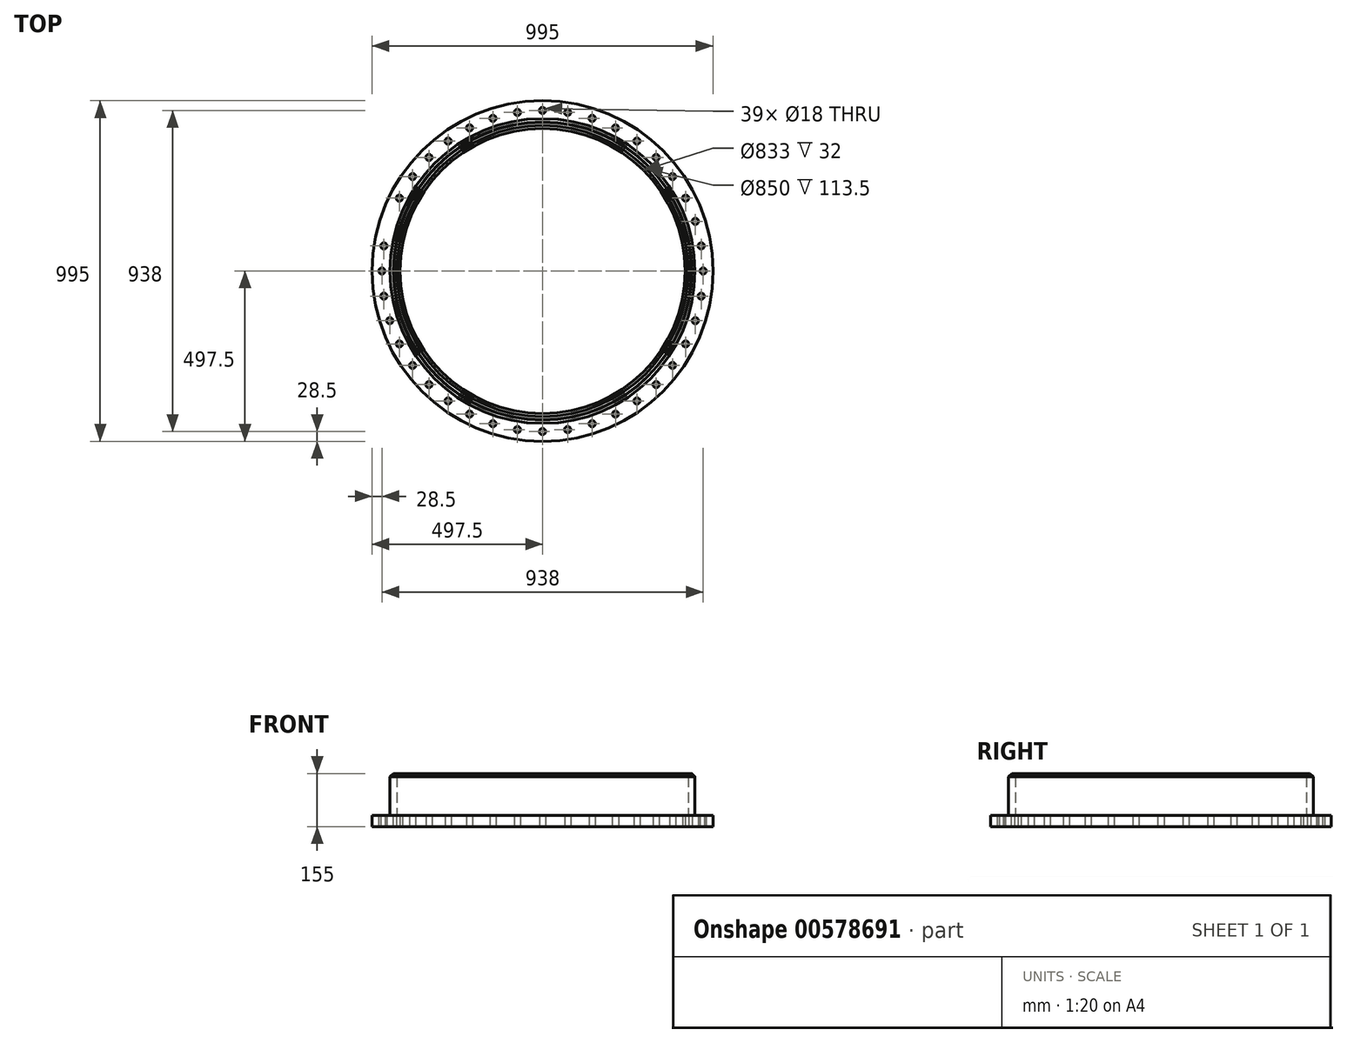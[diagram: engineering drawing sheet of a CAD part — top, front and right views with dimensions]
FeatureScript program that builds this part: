
annotation { "Feature Type Name" : "Feature", "Feature Type Description" : "" }
export const myFeature = defineFeature(function(context is Context, id is Id, definition is map)
    precondition{}
    {
        {
            var Q0;
            Q0=qCreatedBy(makeId("Top.planeOp"),FACE);
            var sketch = newSketch(context, id + "F0", { "sketchPlane" : qUnion([Q0])});
            skCircle(sketch, "E0", {"center": v(0, 0) * mm, "radius": 497.5 * mm});
            skCircle(sketch, "E1", {"center": v(0, 0) * mm, "radius": 416.5 * mm});
            skSolve(sketch);
        }
        {
            var Q0;
            Q0=makeQuery(id+"F0.imprint","IMPRINT",FACE,{"disambiguationData":[TD([[makeQuery(id+"F0.imprint","IMPRINT",EDGE,{"derivedFrom":sQuery(id+"F0.wireOp",EDGE,"E0")}),1.0]])]});
            extrude(context, id + "F1", {"entities" : qUnion([Q0]), "depth" : 32 * mm, "offsetDistance" : 25 * mm});
        }
        {
            var Q0;
            Q0=makeQuery(id+"F1.opExtrude","CAP_FACE",FACE,{"disambiguationData":[OSD([sQuery(id+"F0.wireOp",EDGE,"E0"),sQuery(id+"F0.wireOp",EDGE,"E1")])],"isStart":false});
            var sketch = newSketch(context, id + "F2", { "sketchPlane" : qUnion([Q0])});
            skCircle(sketch, "E2", {"center": v(0, 0) * mm, "radius": 445 * mm});
            skCircle(sketch, "E3.0", {"center": v(0, 0) * mm, "radius": 425 * mm});
            skSolve(sketch);
        }
        {
            var Q0;
            Q0=makeQuery(id+"F2.imprint","IMPRINT",FACE,{"disambiguationData":[TD([[makeQuery(id+"F2.imprint","IMPRINT",EDGE,{"derivedFrom":sQuery(id+"F2.wireOp",EDGE,"E2")}),1.0]])]});
            extrude(context, id + "F3", {"entities" : qUnion([Q0]), "operationType" : NewBodyOperationType.ADD, "depth" : 123 * mm, "offsetDistance" : 25 * mm});
        }
        {
            var Q0;
            Q0=qCreatedBy(makeId("Right.planeOp"),FACE);
            var sketch = newSketch(context, id + "F4", { "sketchPlane" : qUnion([Q0])});
            skLineSegment(sketch, "E4", {"start": v(-445, 32) * mm, "end": v(-445, 155) * mm});
            skPoint(sketch, "E5.0.end.orphan", {"position": v(445, 155) * mm});
            skPoint(sketch, "E5.0.start.orphan", {"position": v(-445, 155) * mm});
            skLineSegment(sketch, "E6", {"start": v(-445, 155) * mm, "end": v(-435.5, 155) * mm});
            skLineSegment(sketch, "E7", {"start": v(-435.5, 155) * mm, "end": v(-445, 145.5) * mm});
            skLineSegment(sketch, "E8", {"start": v(-435, 155) * mm, "end": v(-435, 143.47) * mm, "construction": true});
            skLineSegment(sketch, "E9.MirrorCS", {"start": v(-434.5, 155) * mm, "end": v(-425, 145.5) * mm});
            skLineSegment(sketch, "E10", {"start": v(-445, 145.5) * mm, "end": v(-445, 155) * mm});
            skLineSegment(sketch, "E11", {"start": v(-425, 155) * mm, "end": v(-425, 145.5) * mm});
            skLineSegment(sketch, "E12.trimOffspring", {"start": v(-434.5, 155) * mm, "end": v(-425, 155) * mm});
            skSolve(sketch);
        }
        {
            var Q0;
            Q0=makeQuery(id+"F4.imprint","IMPRINT",FACE,{"disambiguationData":[TD([[makeQuery(id+"F4.imprint","IMPRINT",EDGE,{"derivedFrom":sQuery(id+"F4.wireOp",EDGE,"E6")}),-1.0]])]});
            var Q1;
            Q1=makeQuery(id+"F4.imprint","IMPRINT",FACE,{"disambiguationData":[TD([[makeQuery(id+"F4.imprint","IMPRINT",EDGE,{"derivedFrom":sQuery(id+"F4.wireOp",EDGE,"E9.MirrorCS")}),1.0]])]});
            var Q2;
            Q2=makeQuery(id+"F3.opExtrude","CAP_EDGE",EDGE,{"disambiguationData":[OSD([sQuery(id+"F2.wireOp",EDGE,"E3.0")])],"isStart":false});
            revolve(context, id + "F5", {"operationType" : NewBodyOperationType.REMOVE, "entities" : qUnion([Q0, Q1]), "axis" : qUnion([Q2]), "revolveType" : RevolveType.FULL, "oppositeDirection" : true});
        }
        {
            var Q0;
            Q0=makeQuery(id+"F1.opExtrude","CAP_FACE",FACE,{"disambiguationData":[OSD([sQuery(id+"F0.wireOp",EDGE,"E0"),sQuery(id+"F0.wireOp",EDGE,"E1")])],"isStart":true});
            var sketch = newSketch(context, id + "F6", { "sketchPlane" : qUnion([Q0])});
            skCircle(sketch, "E13", {"center": v(0, 0) * mm, "radius": 469 * mm, "construction": true});
            skCircle(sketch, "E14", {"center": v(0, 469) * mm, "radius": 9 * mm});
            skCircle(sketch, "E15.1.0", {"center": v(-73.37, 463.23) * mm, "radius": 9 * mm});
            skCircle(sketch, "E15.2.0", {"center": v(-144.93, 446.05) * mm, "radius": 9 * mm});
            skCircle(sketch, "E15.3.0", {"center": v(-212.92, 417.88) * mm, "radius": 9 * mm});
            skCircle(sketch, "E15.4.0", {"center": v(-275.67, 379.43) * mm, "radius": 9 * mm});
            skCircle(sketch, "E15.5.0", {"center": v(-331.63, 331.63) * mm, "radius": 9 * mm});
            skCircle(sketch, "E15.6.0", {"center": v(-379.43, 275.67) * mm, "radius": 9 * mm});
            skCircle(sketch, "E15.7.0", {"center": v(-417.88, 212.92) * mm, "radius": 9 * mm});
            skCircle(sketch, "E15.8.0", {"center": v(-446.05, 144.93) * mm, "radius": 9 * mm});
            skCircle(sketch, "E15.9.0", {"center": v(-463.23, 73.37) * mm, "radius": 9 * mm});
            skCircle(sketch, "E15.10.0", {"center": v(-469, 0) * mm, "radius": 9 * mm});
            skCircle(sketch, "E15.11.0", {"center": v(-463.23, -73.37) * mm, "radius": 9 * mm});
            skCircle(sketch, "E15.12.0", {"center": v(-446.05, -144.93) * mm, "radius": 9 * mm});
            skCircle(sketch, "E15.13.0", {"center": v(-417.88, -212.92) * mm, "radius": 9 * mm});
            skCircle(sketch, "E15.14.0", {"center": v(-379.43, -275.67) * mm, "radius": 9 * mm});
            skCircle(sketch, "E15.15.0", {"center": v(-331.63, -331.63) * mm, "radius": 9 * mm});
            skCircle(sketch, "E15.16.0", {"center": v(-275.67, -379.43) * mm, "radius": 9 * mm});
            skCircle(sketch, "E15.17.0", {"center": v(-212.92, -417.88) * mm, "radius": 9 * mm});
            skCircle(sketch, "E15.18.0", {"center": v(-144.93, -446.05) * mm, "radius": 9 * mm});
            skCircle(sketch, "E15.19.0", {"center": v(-73.37, -463.23) * mm, "radius": 9 * mm});
            skCircle(sketch, "E15.20.0", {"center": v(0, -469) * mm, "radius": 9 * mm});
            skCircle(sketch, "E15.21.0", {"center": v(73.37, -463.23) * mm, "radius": 9 * mm});
            skCircle(sketch, "E15.22.0", {"center": v(144.93, -446.05) * mm, "radius": 9 * mm});
            skCircle(sketch, "E15.23.0", {"center": v(212.92, -417.88) * mm, "radius": 9 * mm});
            skCircle(sketch, "E15.24.0", {"center": v(275.67, -379.43) * mm, "radius": 9 * mm});
            skCircle(sketch, "E15.25.0", {"center": v(331.63, -331.63) * mm, "radius": 9 * mm});
            skCircle(sketch, "E15.26.0", {"center": v(379.43, -275.67) * mm, "radius": 9 * mm});
            skCircle(sketch, "E15.27.0", {"center": v(417.88, -212.92) * mm, "radius": 9 * mm});
            skCircle(sketch, "E15.28.0", {"center": v(446.05, -144.93) * mm, "radius": 9 * mm});
            skCircle(sketch, "E15.29.0", {"center": v(463.23, -73.37) * mm, "radius": 9 * mm});
            skCircle(sketch, "E15.30.0", {"center": v(469, 0) * mm, "radius": 9 * mm});
            skCircle(sketch, "E15.31.0", {"center": v(463.23, 73.37) * mm, "radius": 9 * mm});
            skCircle(sketch, "E15.32.0", {"center": v(446.05, 144.93) * mm, "radius": 9 * mm});
            skCircle(sketch, "E15.33.0", {"center": v(417.88, 212.92) * mm, "radius": 9 * mm});
            skCircle(sketch, "E15.34.0", {"center": v(379.43, 275.67) * mm, "radius": 9 * mm});
            skCircle(sketch, "E15.35.0", {"center": v(331.63, 331.63) * mm, "radius": 9 * mm});
            skCircle(sketch, "E15.36.0", {"center": v(275.67, 379.43) * mm, "radius": 9 * mm});
            skCircle(sketch, "E15.37.0", {"center": v(212.92, 417.88) * mm, "radius": 9 * mm});
            skCircle(sketch, "E15.38.0", {"center": v(144.93, 446.05) * mm, "radius": 9 * mm});
            skCircle(sketch, "E15.39.0", {"center": v(73.37, 463.23) * mm, "radius": 9 * mm});
            skSolve(sketch);
        }
        {
            var Q0;
            Q0=makeQuery(id+"F6.imprint","IMPRINT",FACE,{"disambiguationData":[TD([[makeQuery(id+"F6.imprint","IMPRINT",EDGE,{"derivedFrom":sQuery(id+"F6.wireOp",EDGE,"E14")}),1.0]])]});
            var Q1;
            Q1=makeQuery(id+"F6.imprint","IMPRINT",FACE,{"disambiguationData":[TD([[makeQuery(id+"F6.imprint","IMPRINT",EDGE,{"derivedFrom":sQuery(id+"F6.wireOp",EDGE,"E15.39.0")}),1.0]])]});
            var Q2;
            Q2=makeQuery(id+"F6.imprint","IMPRINT",FACE,{"disambiguationData":[TD([[makeQuery(id+"F6.imprint","IMPRINT",EDGE,{"derivedFrom":sQuery(id+"F6.wireOp",EDGE,"E15.38.0")}),1.0]])]});
            var Q3;
            Q3=makeQuery(id+"F6.imprint","IMPRINT",FACE,{"disambiguationData":[TD([[makeQuery(id+"F6.imprint","IMPRINT",EDGE,{"derivedFrom":sQuery(id+"F6.wireOp",EDGE,"E15.37.0")}),1.0]])]});
            var Q4;
            Q4=makeQuery(id+"F6.imprint","IMPRINT",FACE,{"disambiguationData":[TD([[makeQuery(id+"F6.imprint","IMPRINT",EDGE,{"derivedFrom":sQuery(id+"F6.wireOp",EDGE,"E15.36.0")}),1.0]])]});
            var Q5;
            Q5=makeQuery(id+"F6.imprint","IMPRINT",FACE,{"disambiguationData":[TD([[makeQuery(id+"F6.imprint","IMPRINT",EDGE,{"derivedFrom":sQuery(id+"F6.wireOp",EDGE,"E15.35.0")}),1.0]])]});
            var Q6;
            Q6=makeQuery(id+"F6.imprint","IMPRINT",FACE,{"disambiguationData":[TD([[makeQuery(id+"F6.imprint","IMPRINT",EDGE,{"derivedFrom":sQuery(id+"F6.wireOp",EDGE,"E15.34.0")}),1.0]])]});
            var Q7;
            Q7=makeQuery(id+"F6.imprint","IMPRINT",FACE,{"disambiguationData":[TD([[makeQuery(id+"F6.imprint","IMPRINT",EDGE,{"derivedFrom":sQuery(id+"F6.wireOp",EDGE,"E15.33.0")}),1.0]])]});
            var Q8;
            Q8=makeQuery(id+"F6.imprint","IMPRINT",FACE,{"disambiguationData":[TD([[makeQuery(id+"F6.imprint","IMPRINT",EDGE,{"derivedFrom":sQuery(id+"F6.wireOp",EDGE,"E15.32.0")}),1.0]])]});
            var Q9;
            Q9=makeQuery(id+"F6.imprint","IMPRINT",FACE,{"disambiguationData":[TD([[makeQuery(id+"F6.imprint","IMPRINT",EDGE,{"derivedFrom":sQuery(id+"F6.wireOp",EDGE,"E15.31.0")}),1.0]])]});
            var Q10;
            Q10=makeQuery(id+"F6.imprint","IMPRINT",FACE,{"disambiguationData":[TD([[makeQuery(id+"F6.imprint","IMPRINT",EDGE,{"derivedFrom":sQuery(id+"F6.wireOp",EDGE,"E15.30.0")}),1.0]])]});
            var Q11;
            Q11=makeQuery(id+"F6.imprint","IMPRINT",FACE,{"disambiguationData":[TD([[makeQuery(id+"F6.imprint","IMPRINT",EDGE,{"derivedFrom":sQuery(id+"F6.wireOp",EDGE,"E15.29.0")}),1.0]])]});
            var Q12;
            Q12=makeQuery(id+"F6.imprint","IMPRINT",FACE,{"disambiguationData":[TD([[makeQuery(id+"F6.imprint","IMPRINT",EDGE,{"derivedFrom":sQuery(id+"F6.wireOp",EDGE,"E15.28.0")}),1.0]])]});
            var Q13;
            Q13=makeQuery(id+"F6.imprint","IMPRINT",FACE,{"disambiguationData":[TD([[makeQuery(id+"F6.imprint","IMPRINT",EDGE,{"derivedFrom":sQuery(id+"F6.wireOp",EDGE,"E15.27.0")}),1.0]])]});
            var Q14;
            Q14=makeQuery(id+"F6.imprint","IMPRINT",FACE,{"disambiguationData":[TD([[makeQuery(id+"F6.imprint","IMPRINT",EDGE,{"derivedFrom":sQuery(id+"F6.wireOp",EDGE,"E15.26.0")}),1.0]])]});
            var Q15;
            Q15=makeQuery(id+"F6.imprint","IMPRINT",FACE,{"disambiguationData":[TD([[makeQuery(id+"F6.imprint","IMPRINT",EDGE,{"derivedFrom":sQuery(id+"F6.wireOp",EDGE,"E15.25.0")}),1.0]])]});
            var Q16;
            Q16=makeQuery(id+"F6.imprint","IMPRINT",FACE,{"disambiguationData":[TD([[makeQuery(id+"F6.imprint","IMPRINT",EDGE,{"derivedFrom":sQuery(id+"F6.wireOp",EDGE,"E15.24.0")}),1.0]])]});
            var Q17;
            Q17=makeQuery(id+"F6.imprint","IMPRINT",FACE,{"disambiguationData":[TD([[makeQuery(id+"F6.imprint","IMPRINT",EDGE,{"derivedFrom":sQuery(id+"F6.wireOp",EDGE,"E15.23.0")}),1.0]])]});
            var Q18;
            Q18=makeQuery(id+"F6.imprint","IMPRINT",FACE,{"disambiguationData":[TD([[makeQuery(id+"F6.imprint","IMPRINT",EDGE,{"derivedFrom":sQuery(id+"F6.wireOp",EDGE,"E15.22.0")}),1.0]])]});
            var Q19;
            Q19=makeQuery(id+"F6.imprint","IMPRINT",FACE,{"disambiguationData":[TD([[makeQuery(id+"F6.imprint","IMPRINT",EDGE,{"derivedFrom":sQuery(id+"F6.wireOp",EDGE,"E15.21.0")}),1.0]])]});
            var Q20;
            Q20=makeQuery(id+"F6.imprint","IMPRINT",FACE,{"disambiguationData":[TD([[makeQuery(id+"F6.imprint","IMPRINT",EDGE,{"derivedFrom":sQuery(id+"F6.wireOp",EDGE,"E15.20.0")}),1.0]])]});
            var Q21;
            Q21=makeQuery(id+"F6.imprint","IMPRINT",FACE,{"disambiguationData":[TD([[makeQuery(id+"F6.imprint","IMPRINT",EDGE,{"derivedFrom":sQuery(id+"F6.wireOp",EDGE,"E15.19.0")}),1.0]])]});
            var Q22;
            Q22=makeQuery(id+"F6.imprint","IMPRINT",FACE,{"disambiguationData":[TD([[makeQuery(id+"F6.imprint","IMPRINT",EDGE,{"derivedFrom":sQuery(id+"F6.wireOp",EDGE,"E15.18.0")}),1.0]])]});
            var Q23;
            Q23=makeQuery(id+"F6.imprint","IMPRINT",FACE,{"disambiguationData":[TD([[makeQuery(id+"F6.imprint","IMPRINT",EDGE,{"derivedFrom":sQuery(id+"F6.wireOp",EDGE,"E15.17.0")}),1.0]])]});
            var Q24;
            Q24=makeQuery(id+"F6.imprint","IMPRINT",FACE,{"disambiguationData":[TD([[makeQuery(id+"F6.imprint","IMPRINT",EDGE,{"derivedFrom":sQuery(id+"F6.wireOp",EDGE,"E15.16.0")}),1.0]])]});
            var Q25;
            Q25=makeQuery(id+"F6.imprint","IMPRINT",FACE,{"disambiguationData":[TD([[makeQuery(id+"F6.imprint","IMPRINT",EDGE,{"derivedFrom":sQuery(id+"F6.wireOp",EDGE,"E15.15.0")}),1.0]])]});
            var Q26;
            Q26=makeQuery(id+"F6.imprint","IMPRINT",FACE,{"disambiguationData":[TD([[makeQuery(id+"F6.imprint","IMPRINT",EDGE,{"derivedFrom":sQuery(id+"F6.wireOp",EDGE,"E15.14.0")}),1.0]])]});
            var Q27;
            Q27=makeQuery(id+"F6.imprint","IMPRINT",FACE,{"disambiguationData":[TD([[makeQuery(id+"F6.imprint","IMPRINT",EDGE,{"derivedFrom":sQuery(id+"F6.wireOp",EDGE,"E15.13.0")}),1.0]])]});
            var Q28;
            Q28=makeQuery(id+"F6.imprint","IMPRINT",FACE,{"disambiguationData":[TD([[makeQuery(id+"F6.imprint","IMPRINT",EDGE,{"derivedFrom":sQuery(id+"F6.wireOp",EDGE,"E15.11.0")}),1.0]])]});
            var Q29;
            Q29=makeQuery(id+"F6.imprint","IMPRINT",FACE,{"disambiguationData":[TD([[makeQuery(id+"F6.imprint","IMPRINT",EDGE,{"derivedFrom":sQuery(id+"F6.wireOp",EDGE,"E15.10.0")}),1.0]])]});
            var Q30;
            Q30=makeQuery(id+"F6.imprint","IMPRINT",FACE,{"disambiguationData":[TD([[makeQuery(id+"F6.imprint","IMPRINT",EDGE,{"derivedFrom":sQuery(id+"F6.wireOp",EDGE,"E15.9.0")}),1.0]])]});
            var Q31;
            Q31=makeQuery(id+"F6.imprint","IMPRINT",FACE,{"disambiguationData":[TD([[makeQuery(id+"F6.imprint","IMPRINT",EDGE,{"derivedFrom":sQuery(id+"F6.wireOp",EDGE,"E15.8.0")}),1.0]])]});
            var Q32;
            Q32=makeQuery(id+"F6.imprint","IMPRINT",FACE,{"disambiguationData":[TD([[makeQuery(id+"F6.imprint","IMPRINT",EDGE,{"derivedFrom":sQuery(id+"F6.wireOp",EDGE,"E15.7.0")}),1.0]])]});
            var Q33;
            Q33=makeQuery(id+"F6.imprint","IMPRINT",FACE,{"disambiguationData":[TD([[makeQuery(id+"F6.imprint","IMPRINT",EDGE,{"derivedFrom":sQuery(id+"F6.wireOp",EDGE,"E15.6.0")}),1.0]])]});
            var Q34;
            Q34=makeQuery(id+"F6.imprint","IMPRINT",FACE,{"disambiguationData":[TD([[makeQuery(id+"F6.imprint","IMPRINT",EDGE,{"derivedFrom":sQuery(id+"F6.wireOp",EDGE,"E15.5.0")}),1.0]])]});
            var Q35;
            Q35=makeQuery(id+"F6.imprint","IMPRINT",FACE,{"disambiguationData":[TD([[makeQuery(id+"F6.imprint","IMPRINT",EDGE,{"derivedFrom":sQuery(id+"F6.wireOp",EDGE,"E15.4.0")}),1.0]])]});
            var Q36;
            Q36=makeQuery(id+"F6.imprint","IMPRINT",FACE,{"disambiguationData":[TD([[makeQuery(id+"F6.imprint","IMPRINT",EDGE,{"derivedFrom":sQuery(id+"F6.wireOp",EDGE,"E15.3.0")}),1.0]])]});
            var Q37;
            Q37=makeQuery(id+"F6.imprint","IMPRINT",FACE,{"disambiguationData":[TD([[makeQuery(id+"F6.imprint","IMPRINT",EDGE,{"derivedFrom":sQuery(id+"F6.wireOp",EDGE,"E15.2.0")}),1.0]])]});
            var Q38;
            Q38=makeQuery(id+"F6.imprint","IMPRINT",FACE,{"disambiguationData":[TD([[makeQuery(id+"F6.imprint","IMPRINT",EDGE,{"derivedFrom":sQuery(id+"F6.wireOp",EDGE,"E15.1.0")}),1.0]])]});
            extrude(context, id + "F7", {"entities" : qUnion([Q0, Q1, Q2, Q3, Q4, Q5, Q6, Q7, Q8, Q9, Q10, Q11, Q12, Q13, Q14, Q15, Q16, Q17, Q18, Q19, Q20, Q21, Q22, Q23, Q24, Q25, Q26, Q27, Q28, Q29, Q30, Q31, Q32, Q33, Q34, Q35, Q36, Q37, Q38]), "operationType" : NewBodyOperationType.REMOVE, "endBound" : BoundingType.THROUGH_ALL, "oppositeDirection" : true, "depth" : 25 * mm, "offsetDistance" : 25 * mm});
        }
    });
